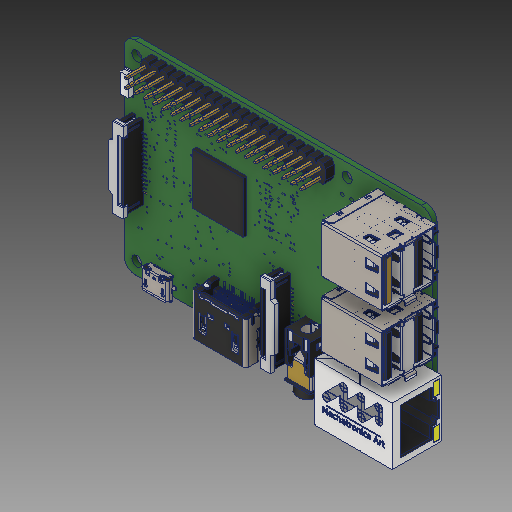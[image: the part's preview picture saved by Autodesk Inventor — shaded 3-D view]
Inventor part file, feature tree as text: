
AUTODESK INVENTOR PART (.ipt)
format: ipt  version: 2018 (Build 220112000, 112)  size: 13,576,192 bytes
history: native  units: mm
features: other x218, sketch x1, projected_geometry x1
ambient origin geometry x8: Origin, YZ Plane, XZ Plane, XY Plane, X Axis, Y Axis, Z Axis, Center Point
bodies: Solid1 (feature_tree), Solid2 (feature_tree), Solid3 (feature_tree), Solid4 (feature_tree), Solid5 (feature_tree), Solid6 (feature_tree), Solid7 (feature_tree), Solid8 (feature_tree), Solid9 (feature_tree), Solid10 (feature_tree), Solid11 (feature_tree), Solid12 (feature_tree), Solid13 (feature_tree), Solid14 (feature_tree), Solid15 (feature_tree), Solid16 (feature_tree), Solid17 (feature_tree), Solid18 (feature_tree), Solid19 (feature_tree), Solid20 (feature_tree), Solid21 (feature_tree), Solid22 (feature_tree), Solid23 (feature_tree), Solid24 (feature_tree), Solid25 (feature_tree), Solid26 (feature_tree), Solid27 (feature_tree), Solid28 (feature_tree), Solid29 (feature_tree), Solid30 (feature_tree), Solid31 (feature_tree), Solid32 (feature_tree), Solid33 (feature_tree), Solid34 (feature_tree), Solid35 (feature_tree), Solid36 (feature_tree), Solid37 (feature_tree), Solid38 (feature_tree), Solid39 (feature_tree), Solid40 (feature_tree), Solid41 (feature_tree), Solid42 (feature_tree), Solid43 (feature_tree), Solid44 (feature_tree), Solid45 (feature_tree), Solid46 (feature_tree), Solid47 (feature_tree), Solid48 (feature_tree), Solid49 (feature_tree), Solid50 (feature_tree), Solid51 (feature_tree), Solid52 (feature_tree), Solid53 (feature_tree), Solid54 (feature_tree), Solid55 (feature_tree), Solid56 (feature_tree), Solid57 (feature_tree), Solid58 (feature_tree), Solid59 (feature_tree), Solid60 (feature_tree), Solid61 (feature_tree), Solid62 (feature_tree), Solid63 (feature_tree), Solid64 (feature_tree), Solid65 (feature_tree), Solid66 (feature_tree), Solid67 (feature_tree), Solid68 (feature_tree), Solid69 (feature_tree), Solid70 (feature_tree), Solid71 (feature_tree), Solid72 (feature_tree), Solid73 (feature_tree), Solid74 (feature_tree), Solid75 (feature_tree), Solid76 (feature_tree), Solid77 (feature_tree), Solid78 (feature_tree), Solid79 (feature_tree), Solid80 (feature_tree), Solid81 (feature_tree), Solid82 (feature_tree), Solid83 (feature_tree), Solid84 (feature_tree), Solid85 (feature_tree), Solid86 (feature_tree), Solid87 (feature_tree), Solid88 (feature_tree), Solid89 (feature_tree), Solid90 (feature_tree), Solid91 (feature_tree), Solid92 (feature_tree), Solid93 (feature_tree), Solid94 (feature_tree), Solid95 (feature_tree), Solid96 (feature_tree), Solid97 (feature_tree), Solid98 (feature_tree), Solid99 (feature_tree), Solid100 (feature_tree), Solid101 (feature_tree), Solid102 (feature_tree), Solid103 (feature_tree), Solid104 (feature_tree), Solid105 (feature_tree), Solid106 (feature_tree), Solid107 (feature_tree), Solid108 (feature_tree), Solid109 (feature_tree), Solid110 (feature_tree), Solid111 (feature_tree), Solid112 (feature_tree), Solid113 (feature_tree), Solid114 (feature_tree), Solid115 (feature_tree), Solid116 (feature_tree), Solid117 (feature_tree), Solid118 (feature_tree), Solid119 (feature_tree), Solid120 (feature_tree), Solid121 (feature_tree), Solid122 (feature_tree), Solid123 (feature_tree), Solid124 (feature_tree), Solid125 (feature_tree), Solid126 (feature_tree), Solid127 (feature_tree), Solid128 (feature_tree), Solid129 (feature_tree), Solid130 (feature_tree), Solid131 (feature_tree), Solid132 (feature_tree), Solid133 (feature_tree), Solid134 (feature_tree), Solid135 (feature_tree), Solid136 (feature_tree), Solid137 (feature_tree), Solid138 (feature_tree), Solid139 (feature_tree), Solid140 (feature_tree), Solid141 (feature_tree), Solid142 (feature_tree), Solid143 (feature_tree), Solid144 (feature_tree), Solid145 (feature_tree), Solid146 (feature_tree), Solid147 (feature_tree), Solid148 (feature_tree), Solid149 (feature_tree), Solid150 (feature_tree), Solid151 (feature_tree), Solid152 (feature_tree), Solid153 (feature_tree), Solid154 (feature_tree), Solid155 (feature_tree), Solid156 (feature_tree), Solid157 (feature_tree), Solid158 (feature_tree), Solid159 (feature_tree), Solid160 (feature_tree), Solid161 (feature_tree), Solid162 (feature_tree), Solid163 (feature_tree), Solid164 (feature_tree), Solid165 (feature_tree), Solid166 (feature_tree), Solid167 (feature_tree), Solid168 (feature_tree), Solid169 (feature_tree), Solid170 (feature_tree), Solid171 (feature_tree), Solid172 (feature_tree), Solid173 (feature_tree), Solid174 (feature_tree), Solid175 (feature_tree), Solid176 (feature_tree), Solid177 (feature_tree), Solid178 (feature_tree), Solid179 (feature_tree), Solid180 (feature_tree), Solid181 (feature_tree), Solid182 (feature_tree), Solid183 (feature_tree), Solid184 (feature_tree), Solid185 (feature_tree), Solid186 (feature_tree), Solid187 (feature_tree), Solid188 (feature_tree), Solid189 (feature_tree), Solid190 (feature_tree), Solid191 (feature_tree), Solid192 (feature_tree), Solid193 (feature_tree), Solid194 (feature_tree), Solid195 (feature_tree), Solid196 (feature_tree), Solid197 (feature_tree), Solid198 (feature_tree), Solid199 (feature_tree), Solid200 (feature_tree), Solid201 (feature_tree), Solid202 (feature_tree), Solid203 (feature_tree), Solid204 (feature_tree), Solid205 (feature_tree), Solid206 (feature_tree), Solid207 (feature_tree), Solid208 (feature_tree), Solid209 (feature_tree), Solid210 (feature_tree), Solid211 (feature_tree), Solid212 (feature_tree), Solid213 (feature_tree), Solid214 (feature_tree), Solid215 (feature_tree), Solid216 (feature_tree), Solid217 (feature_tree)
feature tree (220):
  other  "Raspberry Pi 3 Light Version.STEP"
  sketch  "Sketch1"
  other  "Raspberry Pi 3157-1-solid1"
  other  "Raspberry Pi 3242-1-solid1"
  other  "Raspberry Pi 3266-1-solid1"
  other  "raspberry_pi_3(bar_180_2x20)-2-solid1"
  other  "raspberry_pi_3(bar_180_2x20)-2-solid2"
  other  "raspberry_pi_3(bar_180_2x20)-2-solid3"
  other  "raspberry_pi_3(bar_180_2x20)-2-solid4"
  other  "raspberry_pi_3(bar_180_2x20)-2-solid5"
  other  "raspberry_pi_3(bar_180_2x20)-2-solid6"
  other  "raspberry_pi_3(bar_180_2x20)-2-solid7"
  other  "raspberry_pi_3(bar_180_2x20)-2-solid8"
  other  "raspberry_pi_3(bar_180_2x20)-2-solid9"
  other  "raspberry_pi_3(bar_180_2x20)-2-solid10"
  other  "raspberry_pi_3(bar_180_2x20)-2-solid11"
  other  "raspberry_pi_3(bar_180_2x20)-2-solid12"
  other  "raspberry_pi_3(bar_180_2x20)-2-solid13"
  other  "raspberry_pi_3(bar_180_2x20)-2-solid14"
  other  "raspberry_pi_3(bar_180_2x20)-2-solid15"
  other  "raspberry_pi_3(bar_180_2x20)-2-solid16"
  other  "raspberry_pi_3(bar_180_2x20)-2-solid17"
  other  "raspberry_pi_3(bar_180_2x20)-2-solid18"
  other  "raspberry_pi_3(bar_180_2x20)-2-solid19"
  other  "raspberry_pi_3(bar_180_2x20)-2-solid20"
  other  "raspberry_pi_3(bar_180_2x20)-2-solid21"
  other  "raspberry_pi_3(bar_180_2x20)-2-solid22"
  other  "raspberry_pi_3(bar_180_2x20)-2-solid23"
  other  "raspberry_pi_3(bar_180_2x20)-2-solid24"
  other  "raspberry_pi_3(bar_180_2x20)-2-solid25"
  other  "raspberry_pi_3(bar_180_2x20)-2-solid26"
  other  "raspberry_pi_3(bar_180_2x20)-2-solid27"
  other  "raspberry_pi_3(bar_180_2x20)-2-solid28"
  other  "raspberry_pi_3(bar_180_2x20)-2-solid29"
  other  "raspberry_pi_3(bar_180_2x20)-2-solid30"
  other  "raspberry_pi_3(bar_180_2x20)-2-solid31"
  other  "raspberry_pi_3(bar_180_2x20)-2-solid32"
  other  "raspberry_pi_3(bar_180_2x20)-2-solid33"
  other  "raspberry_pi_3(bar_180_2x20)-2-solid34"
  other  "raspberry_pi_3(bar_180_2x20)-2-solid35"
  other  "raspberry_pi_3(bar_180_2x20)-2-solid36"
  other  "raspberry_pi_3(bar_180_2x20)-2-solid37"
  other  "raspberry_pi_3(bar_180_2x20)-2-solid38"
  other  "raspberry_pi_3(bar_180_2x20)-2-solid39"
  other  "raspberry_pi_3(bar_180_2x20)-2-solid40"
  other  "RPi3_ModelB v1-1_MOLEX_672983090-1-solid1"
  other  "RPi3_ModelB v1-1_MOLEX_672983090-1-solid2"
  other  "RPi3_ModelB v1-1_MOLEX_672983090-1-solid3"
  other  "RPi3_ModelB v1-1_MOLEX_672983090-1-solid4"
  other  "RPi3_ModelB v1-1_MOLEX_672983090-2-solid1"
  other  "RPi3_ModelB v1-1_MOLEX_672983090-2-solid2"
  other  "RPi3_ModelB v1-1_MOLEX_672983090-2-solid3"
  other  "RPi3_ModelB v1-1_MOLEX_672983090-2-solid4"
  other  "RPi3_ModelB v1-1_molex_0473460001-1-solid1"
  other  "RPi3_ModelB v1-1_molex_0473460001-1-solid2"
  other  "RPi3_ModelB v1-1_molex_0473460001-1-solid3"
  other  "RPi3_ModelB v1-1_molex_0471510001-1-solid1"
  other  "RPi3_ModelB v1-1_molex_0471510001-1-solid2"
  other  "RPi3_ModelB v1-1_molex_0471510001-1-solid3"
  other  "RPi3_ModelB v1-1_molex_0471510001-1-solid4"
  other  "RPi3_ModelB v1-1_PJ-322-1-solid1"
  other  "RPi3_ModelB v1-1_PJ-322-1-solid2"
  other  "RPi3_ModelB v1-1_PJ-322-1-solid3"
  other  "RPi3_ModelB v1-1_PJ-322-1-solid4"
  other  "RPi3_ModelB v1-1_PJ-322-1-solid5"
  other  "RPi3_ModelB v1-1_te_1-1734248-5-1-solid1"
  other  "RPi3_ModelB v1-1_te_1-1734248-5-1-solid2"
  other  "RPi3_ModelB v1-1_te_1-1734248-5-1-solid3"
  other  "RPi3_ModelB v1-1_te_1-1734248-5-1-solid4"
  other  "RPi3_ModelB v1-1_te_1-1734248-5-1-solid5"
  other  "RPi3_ModelB v1-1_te_1-1734248-5-1-solid6"
  other  "RPi3_ModelB v1-1_te_1-1734248-5-1-solid7"
  other  "RPi3_ModelB v1-1_te_1-1734248-5-1-solid8"
  other  "RPi3_ModelB v1-1_te_1-1734248-5-1-solid9"
  other  "RPi3_ModelB v1-1_te_1-1734248-5-1-solid10"
  other  "RPi3_ModelB v1-1_te_1-1734248-5-1-solid11"
  other  "RPi3_ModelB v1-1_te_1-1734248-5-1-solid12"
  other  "RPi3_ModelB v1-1_te_1-1734248-5-1-solid13"
  other  "RPi3_ModelB v1-1_te_1-1734248-5-1-solid14"
  other  "RPi3_ModelB v1-1_te_1-1734248-5-1-solid15"
  other  "RPi3_ModelB v1-1_te_1-1734248-5-1-solid16"
  other  "RPi3_ModelB v1-1_te_1-1734248-5-1-solid17"
  other  "RPi3_ModelB v1-1_te_1-1734248-5-2-solid1"
  other  "RPi3_ModelB v1-1_te_1-1734248-5-2-solid2"
  other  "RPi3_ModelB v1-1_te_1-1734248-5-2-solid3"
  other  "RPi3_ModelB v1-1_te_1-1734248-5-2-solid4"
  other  "RPi3_ModelB v1-1_te_1-1734248-5-2-solid5"
  other  "RPi3_ModelB v1-1_te_1-1734248-5-2-solid6"
  other  "RPi3_ModelB v1-1_te_1-1734248-5-2-solid7"
  other  "RPi3_ModelB v1-1_te_1-1734248-5-2-solid8"
  other  "RPi3_ModelB v1-1_te_1-1734248-5-2-solid9"
  other  "RPi3_ModelB v1-1_te_1-1734248-5-2-solid10"
  other  "RPi3_ModelB v1-1_te_1-1734248-5-2-solid11"
  other  "RPi3_ModelB v1-1_te_1-1734248-5-2-solid12"
  other  "RPi3_ModelB v1-1_te_1-1734248-5-2-solid13"
  other  "RPi3_ModelB v1-1_te_1-1734248-5-2-solid14"
  other  "RPi3_ModelB v1-1_te_1-1734248-5-2-solid15"
  other  "RPi3_ModelB v1-1_te_1-1734248-5-2-solid16"
  other  "RPi3_ModelB v1-1_te_1-1734248-5-2-solid17"
  other  "RPi3_ModelB v1-1_MOLEX_1040310811-1-solid1"
  other  "RPi3_ModelB v1-1_MOLEX_1040310811-1-solid2"
  other  "RPi3_ModelB v1-1_MOLEX_1040310811-1-solid3"
  other  "RPi3_ModelB v1-1_MOLEX_1040310811-1-solid4"
  other  "RPi3_ModelB v1-1_MOLEX_1040310811-1-solid5"
  other  "RPi3_ModelB v1-1_MOLEX_1040310811-1-solid6"
  other  "RPi3_ModelB v1-1_MOLEX_1040310811-1-solid7"
  other  "RPi3_ModelB v1-1_MOLEX_1040310811-1-solid8"
  other  "RPi3_ModelB v1-1_MOLEX_1040310811-1-solid9"
  other  "RPi3_ModelB v1-1_MOLEX_1040310811-1-solid10"
  other  "RPi3_ModelB v1-1_raspberry_pi_B_(RJ45)-1-solid1"
  other  "RPi3_ModelB v1-1_raspberry_pi_B_(RJ45)-1-solid2"
  other  "RPi3_ModelB v1-1_raspberry_pi_B_(RJ45)-1-solid3"
  other  "Raspberry Pi 312-1-solid1"
  other  "Raspberry Pi 314-1-solid1"
  other  "Raspberry Pi 3172-1-solid1"
  other  "Raspberry Pi 3173-1-solid1"
  other  "Raspberry Pi 3174-1-solid1"
  other  "Raspberry Pi 3175-1-solid1"
  other  "Raspberry Pi 3176-1-solid1"
  other  "Raspberry Pi 3177-1-solid1"
  other  "Raspberry Pi 3178-1-solid1"
  other  "Raspberry Pi 3179-1-solid1"
  other  "Raspberry Pi 3180-1-solid1"
  other  "Raspberry Pi 3181-1-solid1"
  other  "Raspberry Pi 3182-1-solid1"
  other  "Raspberry Pi 3183-1-solid1"
  other  "Raspberry Pi 3184-1-solid1"
  other  "Raspberry Pi 3185-1-solid1"
  other  "Raspberry Pi 3186-1-solid1"
  other  "Raspberry Pi 3187-1-solid1"
  other  "Raspberry Pi 3188-1-solid1"
  other  "Raspberry Pi 3189-1-solid1"
  other  "Raspberry Pi 3190-1-solid1"
  other  "Raspberry Pi 3191-1-solid1"
  other  "Raspberry Pi 3192-1-solid1"
  other  "Raspberry Pi 3193-1-solid1"
  other  "Raspberry Pi 3194-1-solid1"
  other  "Raspberry Pi 3195-1-solid1"
  other  "Raspberry Pi 3196-1-solid1"
  other  "Raspberry Pi 3197-1-solid1"
  other  "Raspberry Pi 3198-1-solid1"
  other  "Raspberry Pi 3199-1-solid1"
  other  "Raspberry Pi 3200-1-solid1"
  other  "Raspberry Pi 3201-1-solid1"
  other  "Raspberry Pi 3202-1-solid1"
  other  "Raspberry Pi 3203-1-solid1"
  other  "Raspberry Pi 3204-1-solid1"
  other  "Raspberry Pi 3205-1-solid1"
  other  "Raspberry Pi 3206-1-solid1"
  other  "Raspberry Pi 3207-1-solid1"
  other  "Raspberry Pi 3208-1-solid1"
  other  "Raspberry Pi 3209-1-solid1"
  other  "Raspberry Pi 3210-1-solid1"
  other  "Raspberry Pi 3211-1-solid1"
  other  "Raspberry Pi 3212-1-solid1"
  other  "Raspberry Pi 3213-1-solid1"
  other  "Raspberry Pi 3214-1-solid1"
  other  "Raspberry Pi 3215-1-solid1"
  other  "Raspberry Pi 3216-1-solid1"
  other  "Raspberry Pi 3217-1-solid1"
  other  "Raspberry Pi 3218-1-solid1"
  other  "Raspberry Pi 3219-1-solid1"
  other  "Raspberry Pi 3220-1-solid1"
  other  "Raspberry Pi 3221-1-solid1"
  other  "Raspberry Pi 3222-1-solid1"
  other  "Raspberry Pi 3223-1-solid1"
  other  "Raspberry Pi 3224-1-solid1"
  other  "Raspberry Pi 3225-1-solid1"
  other  "Raspberry Pi 3226-1-solid1"
  other  "Raspberry Pi 3227-1-solid1"
  other  "Raspberry Pi 3228-1-solid1"
  other  "Raspberry Pi 3229-1-solid1"
  other  "Raspberry Pi 3230-1-solid1"
  other  "Raspberry Pi 3231-1-solid1"
  other  "Raspberry Pi 3232-1-solid1"
  other  "Raspberry Pi 3233-1-solid1"
  other  "Raspberry Pi 3234-1-solid1"
  other  "Raspberry Pi 3235-1-solid1"
  other  "Raspberry Pi 31-1-solid1"
  other  "Raspberry Pi 36-1-solid1"
  other  "raspberry_pi_B+_(microsd2)-1-solid1"
  other  "Raspberry Pi 3242-2-solid1"
  other  "Raspberry Pi 3242-3-solid1"
  other  "Raspberry Pi 3242-4-solid1"
  other  "Raspberry Pi 3242-5-solid1"
  other  "Raspberry Pi 3242-6-solid1"
  other  "Raspberry Pi 3242-7-solid1"
  other  "Raspberry Pi 3242-8-solid1"
  other  "Raspberry Pi 3242-9-solid1"
  other  "Raspberry Pi 3242-10-solid1"
  other  "Raspberry Pi 3242-11-solid1"
  other  "Raspberry Pi 3242-12-solid1"
  other  "Raspberry Pi 3242-13-solid1"
  other  "Raspberry Pi 3242-14-solid1"
  other  "Raspberry Pi 3242-15-solid1"
  other  "Raspberry Pi 3242-16-solid1"
  other  "Raspberry Pi 3242-17-solid1"
  other  "Raspberry Pi 3242-18-solid1"
  other  "Raspberry Pi 3242-19-solid1"
  other  "Raspberry Pi 3242-20-solid1"
  other  "Raspberry Pi 3266-2-solid1"
  other  "Raspberry Pi 3266-3-solid1"
  other  "Raspberry Pi 3266-4-solid1"
  other  "Raspberry Pi 3266-5-solid1"
  other  "Raspberry Pi 3266-6-solid1"
  other  "Raspberry Pi 3266-7-solid1"
  other  "Raspberry Pi 3266-8-solid1"
  other  "Raspberry Pi 3266-9-solid1"
  other  "Raspberry Pi 3266-10-solid1"
  other  "Raspberry Pi 3266-11-solid1"
  other  "Raspberry Pi 3266-12-solid1"
  other  "Raspberry Pi 3266-13-solid1"
  other  "Raspberry Pi 3266-14-solid1"
  other  "Raspberry Pi 3266-15-solid1"
  other  "Raspberry Pi 3266-16-solid1"
  other  "Raspberry Pi 3266-17-solid1"
  other  "Raspberry Pi 3266-18-solid1"
  other  "Raspberry Pi 3266-19-solid1"
  other  "Raspberry Pi 3266-20-solid1"
  projected_geometry  "Project Cut Edges1"
